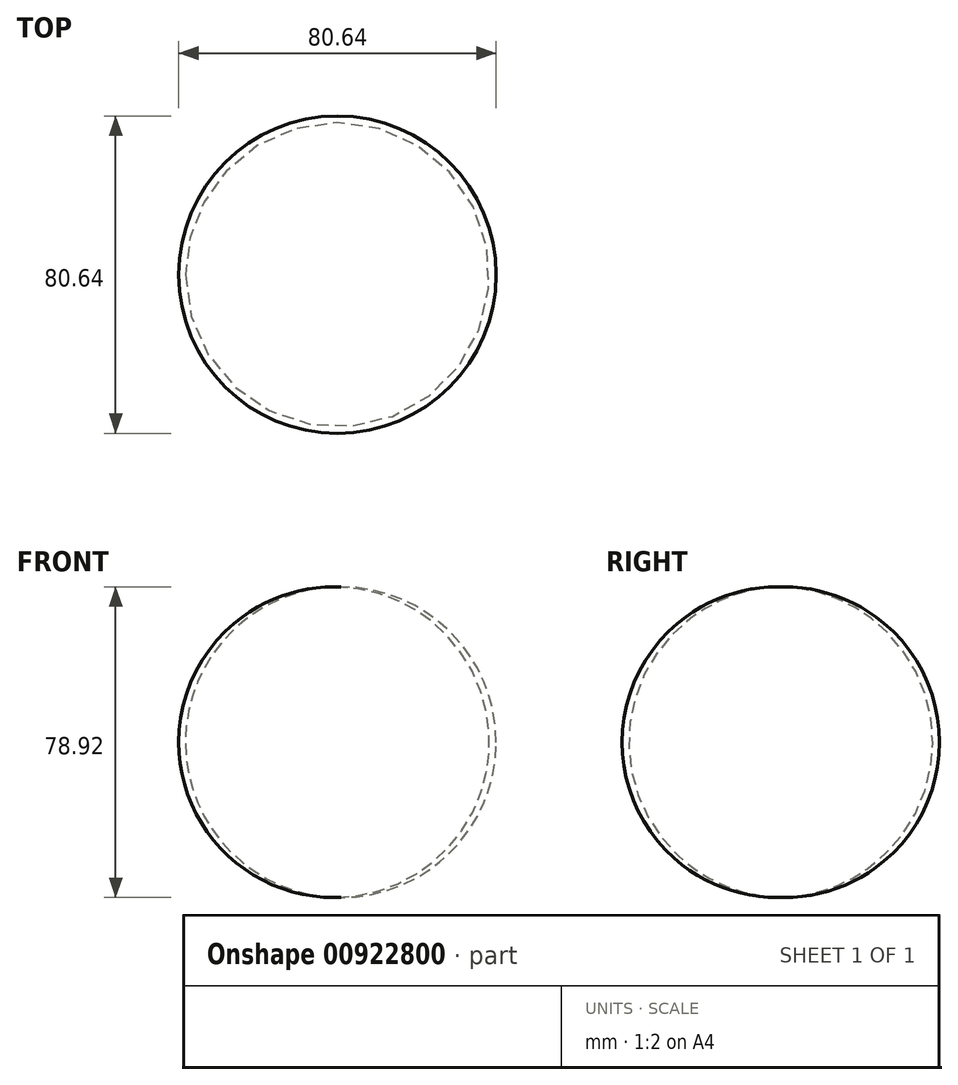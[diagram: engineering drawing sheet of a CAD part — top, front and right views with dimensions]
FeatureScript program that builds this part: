
annotation { "Feature Type Name" : "Feature", "Feature Type Description" : "" }
export const myFeature = defineFeature(function(context is Context, id is Id, definition is map)
    precondition{}
    {
        {
            var Q0;
            Q0=qCreatedBy(makeId("Front.planeOp"),FACE);
            var sketch = newSketch(context, id + "F0", { "sketchPlane" : qUnion([Q0])});
            skLineSegment(sketch, "E0", {"start": v(0, 30.7) * mm, "end": v(0, -48.2) * mm});
            skArc(sketch, "E1", {"start": v(0, -48.2) * mm, "mid": v(40.32, -8.75) * mm, "end": v(0, 30.7) * mm});
            skSolve(sketch);
        }
        {
            var Q0;
            Q0=makeQuery(id+"F0.imprint","IMPRINT",FACE,{"disambiguationData":[TD([[makeQuery(id+"F0.imprint","IMPRINT",EDGE,{"derivedFrom":sQuery(id+"F0.wireOp",EDGE,"E0")}),1.0]])]});
            var Q1;
            Q1=sQuery(id+"F0.wireOp",EDGE,"E0");
            revolve(context, id + "F1", {"surfaceOperationType" : NewSurfaceOperationType.NEW, "entities" : qUnion([Q0]), "axis" : qUnion([Q1]), "revolveType" : RevolveType.FULL});
        }
        {
            var Q0;
            Q0=qCreatedBy(makeId("Top.planeOp"),FACE);
            var sketch = newSketch(context, id + "F2", { "sketchPlane" : qUnion([Q0])});
            skCircle(sketch, "E2", {"center": v(0, 0) * mm, "radius": 3.67 * mm});
            skSolve(sketch);
        }
        {
            var Q0;
            Q0=sQuery(id+"F2.wireOp",EDGE,"E2");
            extrude(context, id + "F3", {"bodyType" : ToolBodyType.SURFACE, "surfaceEntities" : qUnion([Q0]), "depth" : 42.16 * mm, "offsetDistance" : 25.4 * mm});
        }
    });
